# Revit family: JC KONTAKTER JCK201 Armbågskontakt
name_source: partatom
category: Doors
units: mm (PartAtom-declared; Revit-internal decimal feet)

## family parameters
Always vertical = Yes
Cut with Voids When Loaded = No
Host = Wall
Room Calculation Point = No
Shared = No

## types (1)
- Armbågskontakt JCK201
    CE Dokument = https://jckontakter.se
    Cap Finish (Lens) = POM Acetalplast
    Core Finish = Aluminum ENAW 6060
    Default Elevation = 0 mm  [stored 0 ft]
    Description = JCK201 är en modell med inbyggd IR-sensor, som möjliggör beröringsfri funktion. IR-sensorn reagerar på ljusskiftningar, vilket gör att man aktiverar dörröppning genom att bara röra handen framför kontakten.

Denna sortens armbågskontakt är särskilt lämplig i miljöer där man vill begränsa spridning av bakterier, såsom skolor, sjukhus och andra offentliga byggnader.

Modellen är även utrustad med LED-ljus som hjälper till att visa aktuell status- grönt för standby och blått vid aktivering. JCK201 levereras med två relä och en dipswitch som möjliggör ett antal olika installationsalternativ.
    End Cap Finish = POM Tenac C 4520
    Led-ljus = Yes
    Lid Finish = Aluminum ENAW 6060-T6
    Manufacturer = JC Kontakter
    Matning = 7-24V DC-AC
    Model = JCK201
    Placering av armbågskontakt = https://jckontakter.se
    Produktvikt = 0.305 kg
    Sensor = IR-Sensor
    Styrenhet med dipswitch = Yes
    Tekniskt produktblad = https://jckontakter.se
    Tillvalsförteckning = https://jckontakter.se
    Tillverkningsland = Sverige
    URL = https://jckontakter.se
    Utgångar = Två reläer

note: [stored X ft] marks values corroborated as IEEE doubles in the binary element streams (Revit-internal decimal feet)

## geometry (parser evidence)
native form markers: Sweep x4
no freeform markers — native parametric forms only
